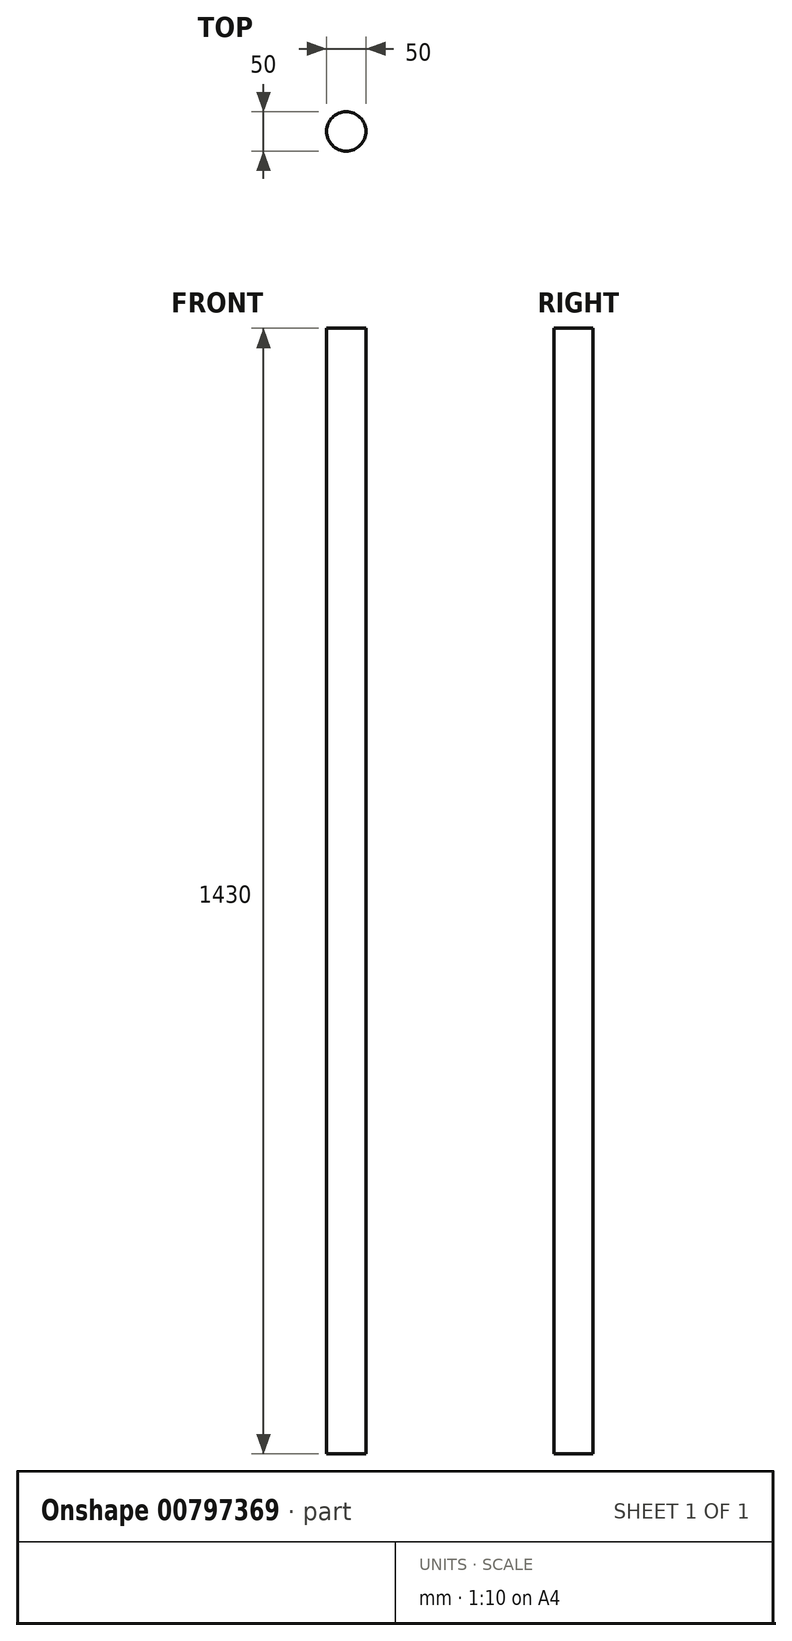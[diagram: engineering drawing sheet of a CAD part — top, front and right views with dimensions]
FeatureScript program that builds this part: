
annotation { "Feature Type Name" : "Feature", "Feature Type Description" : "" }
export const myFeature = defineFeature(function(context is Context, id is Id, definition is map)
    precondition{}
    {
        {
            var Q0;
            Q0=qCreatedBy(makeId("Top.planeOp"),FACE);
            var sketch = newSketch(context, id + "F0", { "sketchPlane" : qUnion([Q0])});
            skCircle(sketch, "E0", {"center": v(0, 0) * mm, "radius": 25 * mm});
            skSolve(sketch);
        }
        {
            var Q0;
            Q0=makeQuery(id+"F0.imprint","IMPRINT",FACE,{"disambiguationData":[TD([[makeQuery(id+"F0.imprint","IMPRINT",EDGE,{"derivedFrom":sQuery(id+"F0.wireOp",EDGE,"E0")}),1.0]])]});
            extrude(context, id + "F1", {"entities" : qUnion([Q0]), "depth" : 1430 * mm, "offsetDistance" : 25 * mm});
        }
    });
